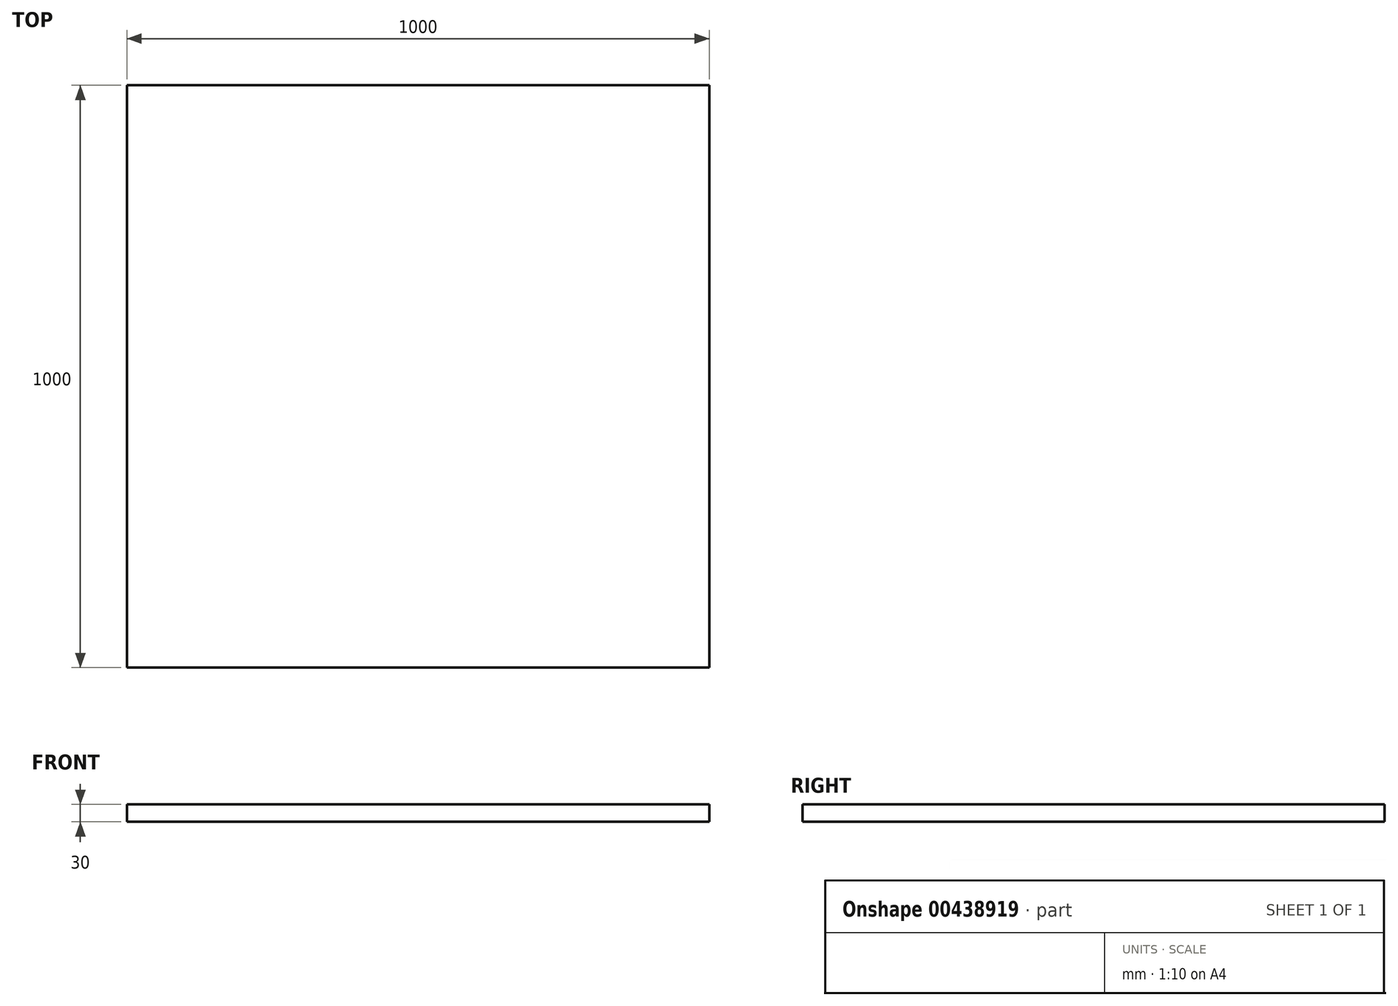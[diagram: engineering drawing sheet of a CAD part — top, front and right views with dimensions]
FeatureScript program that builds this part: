
annotation { "Feature Type Name" : "Feature", "Feature Type Description" : "" }
export const myFeature = defineFeature(function(context is Context, id is Id, definition is map)
    precondition{}
    {
        {
            var Q0;
            Q0=qCreatedBy(makeId("Top.planeOp"),FACE);
            var sketch = newSketch(context, id + "F0", { "sketchPlane" : qUnion([Q0])});
            skLineSegment(sketch, "E0.bottom", {"start": v(-500, -500) * mm, "end": v(500, -500) * mm});
            skLineSegment(sketch, "E0.top", {"start": v(-500, 500) * mm, "end": v(500, 500) * mm});
            skLineSegment(sketch, "E0.left", {"start": v(-500, -500) * mm, "end": v(-500, 500) * mm});
            skLineSegment(sketch, "E0.right", {"start": v(500, -500) * mm, "end": v(500, 500) * mm});
            skPoint(sketch, "E0.middle", {"position": v(0, 0) * mm});
            skSolve(sketch);
        }
        {
            var Q0;
            Q0=makeQuery(id+"F0.imprint","IMPRINT",FACE,{"disambiguationData":[TD([[makeQuery(id+"F0.imprint","IMPRINT",EDGE,{"derivedFrom":sQuery(id+"F0.wireOp",EDGE,"E0.bottom")}),1.0]])]});
            extrude(context, id + "F1", {"entities" : qUnion([Q0]), "depth" : 30 * mm});
        }
    });
